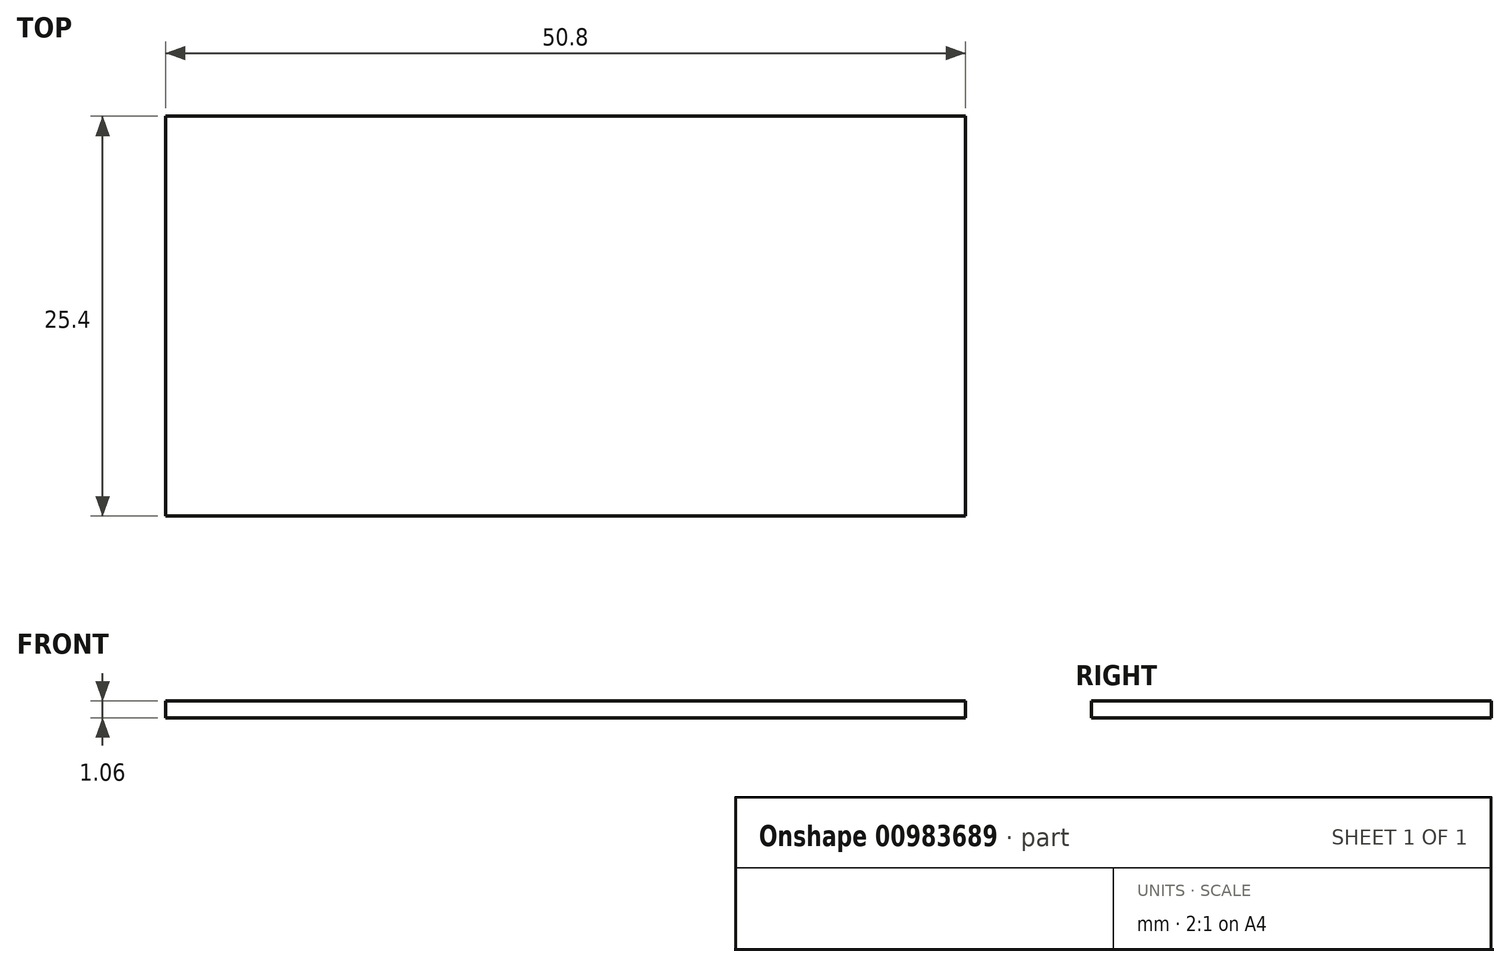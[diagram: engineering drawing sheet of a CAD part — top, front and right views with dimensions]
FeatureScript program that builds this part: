
annotation { "Feature Type Name" : "Feature", "Feature Type Description" : "" }
export const myFeature = defineFeature(function(context is Context, id is Id, definition is map)
    precondition{}
    {
        {
            var Q0;
            Q0=qCreatedBy(makeId("Top.planeOp"),FACE);
            var sketch = newSketch(context, id + "F0", { "sketchPlane" : qUnion([Q0])});
            skLineSegment(sketch, "E0.bottom", {"start": v(25.4, 12.7) * mm, "end": v(-25.4, 12.7) * mm});
            skLineSegment(sketch, "E0.top", {"start": v(25.4, -12.7) * mm, "end": v(-25.4, -12.7) * mm});
            skLineSegment(sketch, "E0.left", {"start": v(25.4, 12.7) * mm, "end": v(25.4, -12.7) * mm});
            skLineSegment(sketch, "E0.right", {"start": v(-25.4, 12.7) * mm, "end": v(-25.4, -12.7) * mm});
            skPoint(sketch, "E0.middle", {"position": v(0, 0) * mm});
            skSolve(sketch);
        }
        {
            var Q0;
            Q0 = qSketchRegion(id + "F0", true);
            extrude(context, id + "F1", {"entities" : qUnion([Q0]), "depth" : 1.06 * mm, "offsetDistance" : 25.4 * mm});
        }
    });
